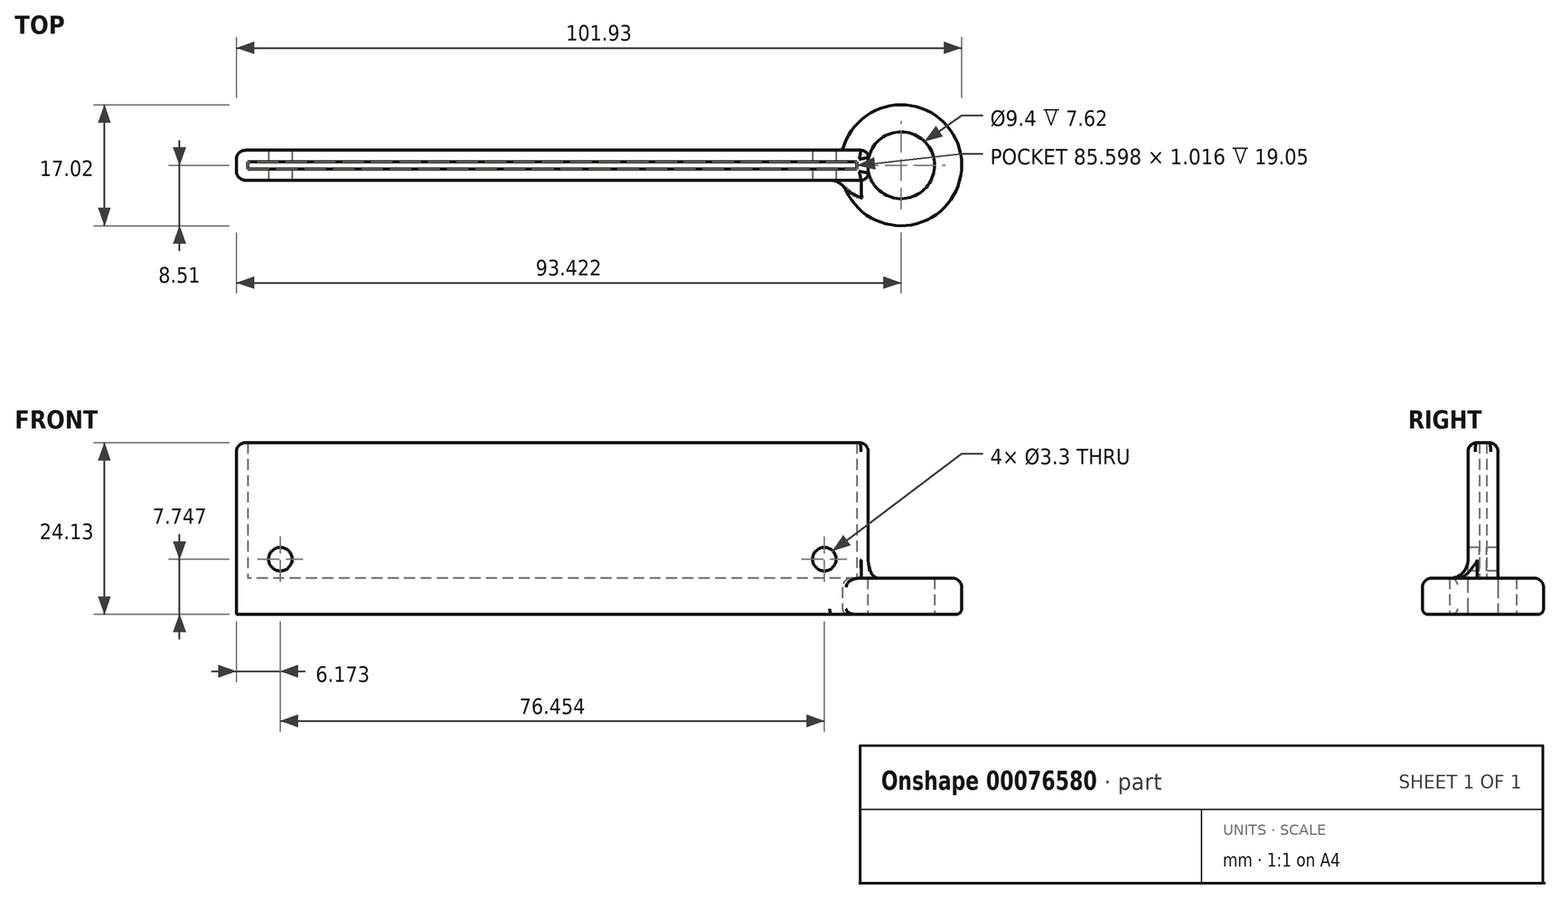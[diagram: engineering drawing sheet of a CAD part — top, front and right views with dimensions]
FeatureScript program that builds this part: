
annotation { "Feature Type Name" : "Feature", "Feature Type Description" : "" }
export const myFeature = defineFeature(function(context is Context, id is Id, definition is map)
    precondition{}
    {
        {
            var Q0;
            Q0=qCreatedBy(makeId("Top.planeOp"),FACE);
            var sketch = newSketch(context, id + "F0", { "sketchPlane" : qUnion([Q0])});
            skLineSegment(sketch, "E0.rect.bottom", {"start": v(42.8, -0.5) * mm, "end": v(-42.8, -0.5) * mm});
            skLineSegment(sketch, "E0.rect.top", {"start": v(42.8, 0.5) * mm, "end": v(-42.8, 0.5) * mm});
            skLineSegment(sketch, "E0.rect.left", {"start": v(42.8, -0.5) * mm, "end": v(42.8, 0.5) * mm});
            skLineSegment(sketch, "E0.rect.right", {"start": v(-42.8, -0.5) * mm, "end": v(-42.8, 0.5) * mm});
            skPoint(sketch, "E0.rect.middle", {"position": v(0, 0) * mm});
            skLineSegment(sketch, "E1.rect.bottom", {"start": v(44.4, -2.1) * mm, "end": v(-44.4, -2.1) * mm});
            skLineSegment(sketch, "E1.rect.top", {"start": v(44.4, 2.1) * mm, "end": v(-44.4, 2.1) * mm});
            skLineSegment(sketch, "E1.rect.left", {"start": v(44.4, -2.1) * mm, "end": v(44.4, 2.1) * mm});
            skLineSegment(sketch, "E1.rect.right", {"start": v(-44.4, -2.1) * mm, "end": v(-44.4, 2.1) * mm});
            skSolve(sketch);
        }
        {
            var Q0;
            Q0=qCreatedBy(makeId("Top.planeOp"),FACE);
            var sketch = newSketch(context, id + "F1", { "sketchPlane" : qUnion([Q0])});
            skLineSegment(sketch, "E2.rect.bottom", {"start": v(-44.4, -2.1) * mm, "end": v(40.78, -2.1) * mm});
            skLineSegment(sketch, "E2.rect.top", {"start": v(-44.4, 2.1) * mm, "end": v(40.78, 2.1) * mm});
            skLineSegment(sketch, "E2.rect.left", {"start": v(-44.4, -2.1) * mm, "end": v(-44.4, 2.1) * mm});
            skPoint(sketch, "E2.rect.middle", {"position": v(0, 0) * mm});
            skCircle(sketch, "E3", {"center": v(49.02, 0) * mm, "radius": 4.7 * mm});
            skArc(sketch, "E4", {"start": v(40.78, -2.1) * mm, "mid": v(57.53, 0) * mm, "end": v(40.78, 2.1) * mm});
            skPoint(sketch, "E5.orphan", {"position": v(44.4, -2.1) * mm});
            skPoint(sketch, "E2.rect.right.end.orphan", {"position": v(44.4, 2.1) * mm});
            skSolve(sketch);
        }
        {
            var Q0;
            Q0=qSketchRegion(id+"F1",true);
            extrude(context, id + "F2", {"entities" : qUnion([Q0]), "depth" : 5.08 * mm});
        }
        {
            var Q0;
            Q0=makeQuery(id+"F2.opExtrude","CAP_FACE",FACE,{"disambiguationData":[OSD([sQuery(id+"F1.wireOp",EDGE,"E2.rect.bottom"),sQuery(id+"F1.wireOp",EDGE,"E2.rect.top"),sQuery(id+"F1.wireOp",EDGE,"E2.rect.left"),sQuery(id+"F1.wireOp",EDGE,"E3"),sQuery(id+"F1.wireOp",EDGE,"E4")])],"isStart":false});
            var sketch = newSketch(context, id + "F3", { "sketchPlane" : qUnion([Q0])});
            skLineSegment(sketch, "E6.rect.bottom", {"start": v(42.8, -0.5) * mm, "end": v(-42.8, -0.5) * mm});
            skLineSegment(sketch, "E6.rect.top", {"start": v(42.8, 0.5) * mm, "end": v(-42.8, 0.5) * mm});
            skLineSegment(sketch, "E6.rect.left", {"start": v(42.8, -0.5) * mm, "end": v(42.8, 0.5) * mm});
            skLineSegment(sketch, "E6.rect.right", {"start": v(-42.8, -0.5) * mm, "end": v(-42.8, 0.5) * mm});
            skPoint(sketch, "E6.rect.middle", {"position": v(0, 0) * mm});
            skLineSegment(sketch, "E7.rect.bottom", {"start": v(44.4, -2.1) * mm, "end": v(-44.4, -2.1) * mm});
            skLineSegment(sketch, "E7.rect.top", {"start": v(44.4, 2.1) * mm, "end": v(-44.4, 2.1) * mm});
            skLineSegment(sketch, "E7.rect.left", {"start": v(44.4, -2.1) * mm, "end": v(44.4, 2.1) * mm});
            skLineSegment(sketch, "E7.rect.right", {"start": v(-44.4, -2.1) * mm, "end": v(-44.4, 2.1) * mm});
            skSolve(sketch);
        }
        {
            var Q0;
            Q0=qSketchRegion(id+"F3",true);
            extrude(context, id + "F4", {"entities" : qUnion([Q0]), "operationType" : NewBodyOperationType.ADD, "depth" : 19.05 * mm});
        }
        {
            var Q0;
            Q0=makeQuery(id+"F2.opExtrude","CAP_EDGE",EDGE,{"disambiguationData":[OSD([sQuery(id+"F1.wireOp",EDGE,"E4")])],"isStart":false});
            fillet(context, id + "F5", {"entities" : qUnion([Q0]), "radius" : 1.27 * mm, "tangentPropagation" : true, "allowEdgeOverflow" : false});
        }
        {
            var Q0;
            Q0=makeQuery(id+"F2.opExtrude","CAP_EDGE",EDGE,{"disambiguationData":[OSD([sQuery(id+"F1.wireOp",EDGE,"E4")])],"isStart":true});
            fillet(context, id + "F6", {"entities" : qUnion([Q0]), "radius" : 0.76 * mm, "tangentPropagation" : true, "allowEdgeOverflow" : false});
        }
        {
            var Q0;
            Q0=makeQuery(id+"F4.opExtrude","SWEPT_EDGE",EDGE,{"disambiguationData":[OSD([sQuery(id+"F3.wireOp",EDGE,"E7.rect.bottom"),sQuery(id+"F3.wireOp",EDGE,"E7.rect.left")])]});
            var Q1;
            Q1=makeQuery(id+"F4.opExtrude","SWEPT_EDGE",EDGE,{"disambiguationData":[OSD([sQuery(id+"F3.wireOp",EDGE,"E7.rect.top"),sQuery(id+"F3.wireOp",EDGE,"E7.rect.left")])]});
            fillet(context, id + "F7", {"entities" : qUnion([Q0, Q1]), "radius" : 1.02 * mm, "tangentPropagation" : true, "allowEdgeOverflow" : false});
        }
        {
            var Q0;
            Q0=makeQuery(id+"F4.opExtrude","CAP_EDGE",EDGE,{"disambiguationData":[OSD([sQuery(id+"F3.wireOp",EDGE,"E7.rect.bottom")])],"isStart":false});
            var Q1;
            Q1=makeQuery(id+"F4.boolean.opBoolean","MERGE",EDGE,{"derivedFrom":[makeQuery(id+"F2.opExtrude","SWEPT_EDGE",EDGE,{"disambiguationData":[OSD([sQuery(id+"F1.wireOp",EDGE,"E2.rect.bottom"),sQuery(id+"F1.wireOp",EDGE,"E2.rect.left")])]}),makeQuery(id+"F4.opExtrude","SWEPT_EDGE",EDGE,{"disambiguationData":[OSD([sQuery(id+"F3.wireOp",EDGE,"E7.rect.bottom"),sQuery(id+"F3.wireOp",EDGE,"E7.rect.right")])]})]});
            fillet(context, id + "F8", {"entities" : qUnion([Q0, Q1]), "radius" : 1.27 * mm, "tangentPropagation" : true, "allowEdgeOverflow" : false});
        }
        {
            var Q0;
            Q0=makeQuery(id+"F4.opExtrude","CAP_EDGE",EDGE,{"disambiguationData":[OSD([sQuery(id+"F3.wireOp",EDGE,"E7.rect.right")])],"isStart":false});
            var Q1;
            Q1=makeQuery(id+"F4.boolean.opBoolean","MERGE",EDGE,{"derivedFrom":[makeQuery(id+"F2.opExtrude","SWEPT_EDGE",EDGE,{"disambiguationData":[OSD([sQuery(id+"F1.wireOp",EDGE,"E2.rect.top"),sQuery(id+"F1.wireOp",EDGE,"E2.rect.left")])]}),makeQuery(id+"F4.opExtrude","SWEPT_EDGE",EDGE,{"disambiguationData":[OSD([sQuery(id+"F3.wireOp",EDGE,"E7.rect.top"),sQuery(id+"F3.wireOp",EDGE,"E7.rect.right")])]})]});
            fillet(context, id + "F9", {"entities" : qUnion([Q0, Q1]), "radius" : 1.27 * mm, "tangentPropagation" : true, "allowEdgeOverflow" : false});
        }
        {
            var Q0;
            Q0=makeQuery(id+"F4.boolean.opBoolean","MERGE",FACE,{"derivedFrom":[makeQuery(id+"F2.opExtrude","SWEPT_FACE",FACE,{"disambiguationData":[OSD([sQuery(id+"F1.wireOp",EDGE,"E2.rect.bottom")])]}),makeQuery(id+"F4.opExtrude","SWEPT_FACE",FACE,{"disambiguationData":[OSD([sQuery(id+"F3.wireOp",EDGE,"E7.rect.bottom")])]})]});
            var sketch = newSketch(context, id + "F10", { "sketchPlane" : qUnion([Q0])});
            skLineSegment(sketch, "E8", {"start": v(-38.23, 0) * mm, "end": v(-38.23, 22.86) * mm, "construction": true});
            skLineSegment(sketch, "E9", {"start": v(38.23, 0) * mm, "end": v(38.23, 22.86) * mm, "construction": true});
            skCircle(sketch, "E10", {"center": v(-38.23, 7.75) * mm, "radius": 1.65 * mm});
            skCircle(sketch, "E11", {"center": v(38.23, 7.75) * mm, "radius": 1.65 * mm});
            skSolve(sketch);
        }
        {
            var Q0;
            Q0=qSketchRegion(id+"F10",true);
            extrude(context, id + "F11", {"entities" : qUnion([Q0]), "operationType" : NewBodyOperationType.REMOVE, "endBound" : BoundingType.THROUGH_ALL, "oppositeDirection" : true, "depth" : 25.4 * mm});
        }
        {
            var Q0;
            Q0=makeQuery(id+"F2.opExtrude","SWEPT_EDGE",EDGE,{"disambiguationData":[OSD([sQuery(id+"F1.wireOp",EDGE,"E2.rect.bottom"),sQuery(id+"F1.wireOp",EDGE,"E4")])]});
            fillet(context, id + "F12", {"entities" : qUnion([Q0]), "radius" : 2.54 * mm, "tangentPropagation" : true, "allowEdgeOverflow" : false});
        }
    });
